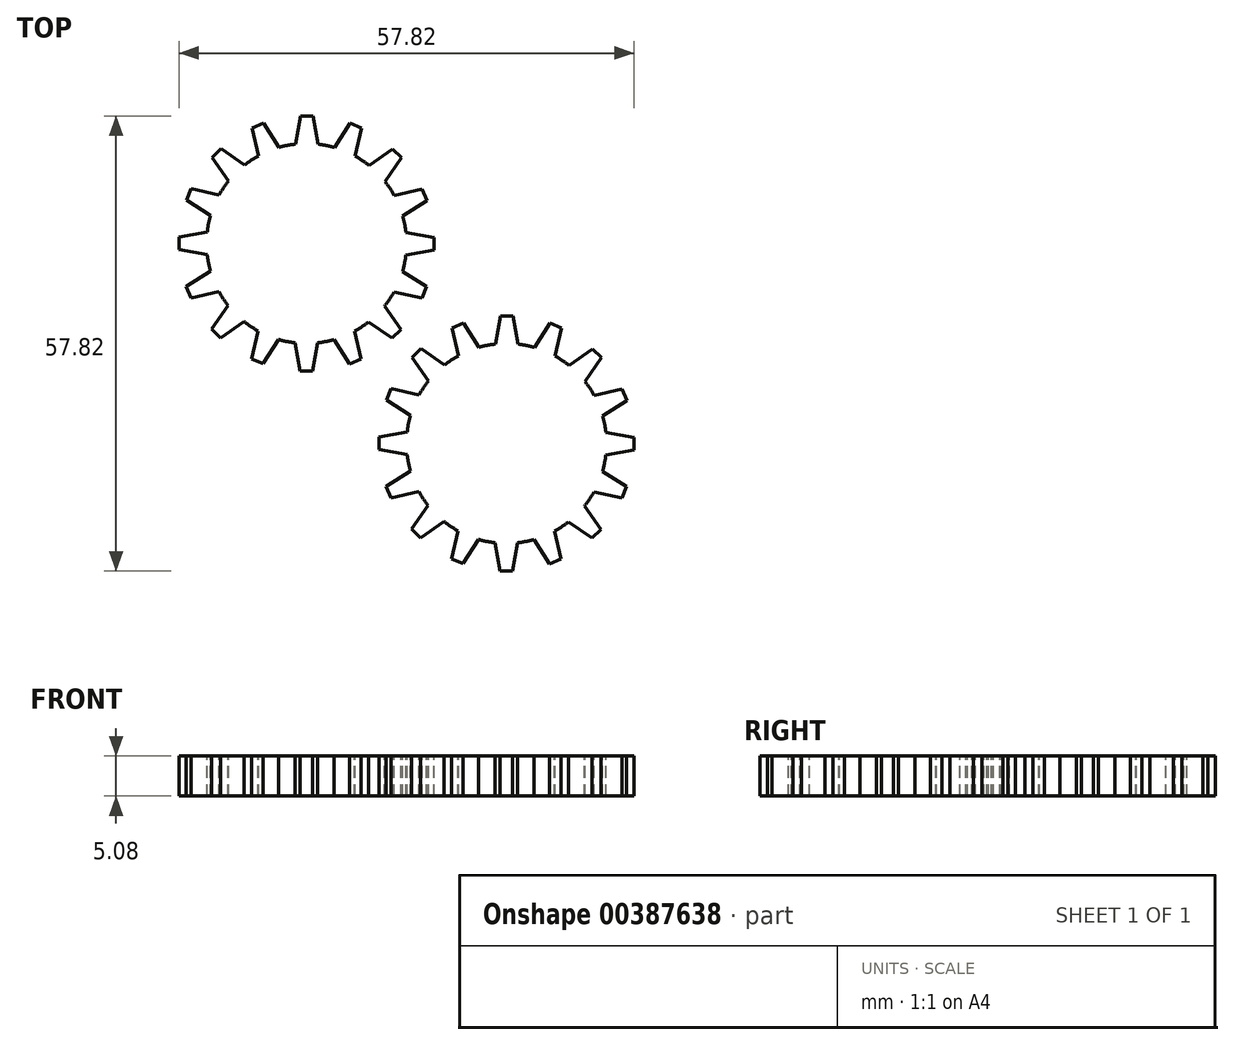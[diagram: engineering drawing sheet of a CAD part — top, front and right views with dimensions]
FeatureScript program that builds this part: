
annotation { "Feature Type Name" : "Feature", "Feature Type Description" : "" }
export const myFeature = defineFeature(function(context is Context, id is Id, definition is map)
    precondition{}
    {
        {
            var Q0;
            Q0=qCreatedBy(makeId("Top.planeOp"),FACE);
            var sketch = newSketch(context, id + "F0", { "sketchPlane" : qUnion([Q0])});
            skArc(sketch, "E0", {"start": v(-6.12, 11.13) * mm, "mid": v(-7.03, 10.58) * mm, "end": v(-7.9, 9.95) * mm});
            skLineSegment(sketch, "E1", {"start": v(-1.4, 12.62) * mm, "end": v(-0.76, 16.2) * mm});
            skLineSegment(sketch, "E2", {"start": v(-0.76, 16.2) * mm, "end": v(0.82, 16.2) * mm});
            skLineSegment(sketch, "E3", {"start": v(0.82, 16.2) * mm, "end": v(1.45, 12.62) * mm});
            skLineSegment(sketch, "E4.1.0", {"start": v(-6.12, 11.13) * mm, "end": v(-6.9, 14.68) * mm});
            skLineSegment(sketch, "E4.1.1", {"start": v(-6.9, 14.68) * mm, "end": v(-5.45, 15.29) * mm});
            skLineSegment(sketch, "E4.1.2", {"start": v(-5.45, 15.29) * mm, "end": v(-3.49, 12.21) * mm});
            skLineSegment(sketch, "E4.2.0", {"start": v(-9.91, 7.94) * mm, "end": v(-12, 10.92) * mm});
            skLineSegment(sketch, "E4.2.1", {"start": v(-12, 10.92) * mm, "end": v(-10.88, 12.04) * mm});
            skLineSegment(sketch, "E4.2.2", {"start": v(-10.88, 12.04) * mm, "end": v(-7.9, 9.95) * mm});
            skLineSegment(sketch, "E5.1.3.0", {"start": v(-12.2, 3.54) * mm, "end": v(-15.27, 5.5) * mm});
            skLineSegment(sketch, "E5.3.3.0", {"start": v(-15.27, 5.5) * mm, "end": v(-14.66, 6.96) * mm});
            skLineSegment(sketch, "E5.6.3.0", {"start": v(-14.66, 6.96) * mm, "end": v(-11.1, 6.17) * mm});
            skLineSegment(sketch, "E5.1.4.0", {"start": v(-12.62, -1.4) * mm, "end": v(-16.2, -0.76) * mm});
            skLineSegment(sketch, "E5.3.4.0", {"start": v(-16.2, -0.76) * mm, "end": v(-16.2, 0.82) * mm});
            skLineSegment(sketch, "E5.6.4.0", {"start": v(-16.2, 0.82) * mm, "end": v(-12.62, 1.45) * mm});
            skLineSegment(sketch, "E5.1.5.0", {"start": v(-11.13, -6.12) * mm, "end": v(-14.68, -6.9) * mm});
            skLineSegment(sketch, "E5.3.5.0", {"start": v(-14.68, -6.9) * mm, "end": v(-15.29, -5.45) * mm});
            skLineSegment(sketch, "E5.6.5.0", {"start": v(-15.29, -5.45) * mm, "end": v(-12.21, -3.49) * mm});
            skLineSegment(sketch, "E6.1.6.0", {"start": v(-7.94, -9.91) * mm, "end": v(-10.92, -12) * mm});
            skLineSegment(sketch, "E6.3.6.0", {"start": v(-10.92, -12) * mm, "end": v(-12.04, -10.88) * mm});
            skLineSegment(sketch, "E6.6.6.0", {"start": v(-12.04, -10.88) * mm, "end": v(-9.95, -7.9) * mm});
            skLineSegment(sketch, "E6.1.7.0", {"start": v(-3.54, -12.2) * mm, "end": v(-5.5, -15.27) * mm});
            skLineSegment(sketch, "E6.3.7.0", {"start": v(-5.5, -15.27) * mm, "end": v(-6.96, -14.66) * mm});
            skLineSegment(sketch, "E6.6.7.0", {"start": v(-6.96, -14.66) * mm, "end": v(-6.17, -11.1) * mm});
            skLineSegment(sketch, "E6.1.8.0", {"start": v(1.4, -12.62) * mm, "end": v(0.76, -16.2) * mm});
            skLineSegment(sketch, "E6.3.8.0", {"start": v(0.76, -16.2) * mm, "end": v(-0.82, -16.2) * mm});
            skLineSegment(sketch, "E6.6.8.0", {"start": v(-0.82, -16.2) * mm, "end": v(-1.45, -12.62) * mm});
            skLineSegment(sketch, "E6.1.9.0", {"start": v(6.12, -11.13) * mm, "end": v(6.9, -14.68) * mm});
            skLineSegment(sketch, "E6.3.9.0", {"start": v(6.9, -14.68) * mm, "end": v(5.45, -15.29) * mm});
            skLineSegment(sketch, "E6.6.9.0", {"start": v(5.45, -15.29) * mm, "end": v(3.49, -12.21) * mm});
            skLineSegment(sketch, "E6.1.10.0", {"start": v(9.91, -7.94) * mm, "end": v(12, -10.92) * mm});
            skLineSegment(sketch, "E6.3.10.0", {"start": v(12, -10.92) * mm, "end": v(10.88, -12.04) * mm});
            skLineSegment(sketch, "E6.6.10.0", {"start": v(10.88, -12.04) * mm, "end": v(7.9, -9.95) * mm});
            skLineSegment(sketch, "E6.1.11.0", {"start": v(12.2, -3.54) * mm, "end": v(15.27, -5.5) * mm});
            skLineSegment(sketch, "E6.3.11.0", {"start": v(15.27, -5.5) * mm, "end": v(14.66, -6.96) * mm});
            skLineSegment(sketch, "E6.6.11.0", {"start": v(14.66, -6.96) * mm, "end": v(11.1, -6.17) * mm});
            skLineSegment(sketch, "E6.1.12.0", {"start": v(12.62, 1.4) * mm, "end": v(16.2, 0.76) * mm});
            skLineSegment(sketch, "E6.3.12.0", {"start": v(16.2, 0.76) * mm, "end": v(16.2, -0.82) * mm});
            skLineSegment(sketch, "E6.6.12.0", {"start": v(16.2, -0.82) * mm, "end": v(12.62, -1.45) * mm});
            skLineSegment(sketch, "E6.1.13.0", {"start": v(11.13, 6.12) * mm, "end": v(14.68, 6.9) * mm});
            skLineSegment(sketch, "E6.3.13.0", {"start": v(14.68, 6.9) * mm, "end": v(15.29, 5.45) * mm});
            skLineSegment(sketch, "E6.6.13.0", {"start": v(15.29, 5.45) * mm, "end": v(12.21, 3.49) * mm});
            skLineSegment(sketch, "E6.1.14.0", {"start": v(7.94, 9.91) * mm, "end": v(10.92, 12) * mm});
            skLineSegment(sketch, "E6.3.14.0", {"start": v(10.92, 12) * mm, "end": v(12.04, 10.88) * mm});
            skLineSegment(sketch, "E6.6.14.0", {"start": v(12.04, 10.88) * mm, "end": v(9.95, 7.9) * mm});
            skLineSegment(sketch, "E6.1.15.0", {"start": v(3.54, 12.2) * mm, "end": v(5.5, 15.27) * mm});
            skLineSegment(sketch, "E6.3.15.0", {"start": v(5.5, 15.27) * mm, "end": v(6.96, 14.66) * mm});
            skLineSegment(sketch, "E6.6.15.0", {"start": v(6.96, 14.66) * mm, "end": v(6.17, 11.1) * mm});
            skArc(sketch, "E7.trimOffspring", {"start": v(-9.91, 7.94) * mm, "mid": v(-10.54, 7.08) * mm, "end": v(-11.1, 6.17) * mm});
            skArc(sketch, "E8.trimOffspring", {"start": v(-12.2, 3.54) * mm, "mid": v(-12.45, 2.5) * mm, "end": v(-12.62, 1.45) * mm});
            skArc(sketch, "E9.trimOffspring", {"start": v(-12.62, -1.4) * mm, "mid": v(-12.46, -2.45) * mm, "end": v(-12.21, -3.49) * mm});
            skArc(sketch, "E10.trimOffspring", {"start": v(-11.13, -6.12) * mm, "mid": v(-10.58, -7.03) * mm, "end": v(-9.95, -7.9) * mm});
            skArc(sketch, "E11.trimOffspring", {"start": v(-7.94, -9.91) * mm, "mid": v(-7.08, -10.54) * mm, "end": v(-6.17, -11.1) * mm});
            skArc(sketch, "E12.trimOffspring", {"start": v(-3.54, -12.2) * mm, "mid": v(-2.5, -12.45) * mm, "end": v(-1.45, -12.62) * mm});
            skArc(sketch, "E13.trimOffspring", {"start": v(1.4, -12.62) * mm, "mid": v(2.45, -12.46) * mm, "end": v(3.49, -12.21) * mm});
            skArc(sketch, "E14.trimOffspring", {"start": v(6.12, -11.13) * mm, "mid": v(7.03, -10.58) * mm, "end": v(7.9, -9.95) * mm});
            skArc(sketch, "E15.trimOffspring", {"start": v(9.91, -7.94) * mm, "mid": v(10.54, -7.08) * mm, "end": v(11.1, -6.17) * mm});
            skArc(sketch, "E16.trimOffspring", {"start": v(12.2, -3.54) * mm, "mid": v(12.45, -2.5) * mm, "end": v(12.62, -1.45) * mm});
            skArc(sketch, "E17.trimOffspring", {"start": v(12.62, 1.4) * mm, "mid": v(12.46, 2.45) * mm, "end": v(12.21, 3.49) * mm});
            skArc(sketch, "E18.trimOffspring", {"start": v(11.13, 6.12) * mm, "mid": v(10.58, 7.03) * mm, "end": v(9.95, 7.9) * mm});
            skArc(sketch, "E19.trimOffspring", {"start": v(7.94, 9.91) * mm, "mid": v(7.08, 10.54) * mm, "end": v(6.17, 11.1) * mm});
            skArc(sketch, "E20.trimOffspring", {"start": v(3.54, 12.2) * mm, "mid": v(2.5, 12.45) * mm, "end": v(1.45, 12.62) * mm});
            skArc(sketch, "E21.trimOffspring", {"start": v(-1.4, 12.62) * mm, "mid": v(-2.45, 12.46) * mm, "end": v(-3.49, 12.21) * mm});
            skSolve(sketch);
        }
        {
            var Q0;
            Q0 = qSketchRegion(id + "F0", true);
            var Q1;
            Q1=sQuery(id+"F0.wireOp",EDGE,"E4.2.2");
            var Q2;
            Q2=sQuery(id+"F0.wireOp",EDGE,"E4.2.1");
            var Q3;
            Q3=sQuery(id+"F0.wireOp",EDGE,"E4.2.0");
            var Q4;
            Q4=sQuery(id+"F0.wireOp",EDGE,"E7.trimOffspring");
            var Q5;
            Q5=sQuery(id+"F0.wireOp",EDGE,"E5.6.3.0");
            var Q6;
            Q6=sQuery(id+"F0.wireOp",EDGE,"E5.3.3.0");
            var Q7;
            Q7=sQuery(id+"F0.wireOp",EDGE,"E5.1.3.0");
            var Q8;
            Q8=sQuery(id+"F0.wireOp",EDGE,"E8.trimOffspring");
            var Q9;
            Q9=sQuery(id+"F0.wireOp",EDGE,"E5.6.4.0");
            var Q10;
            Q10=sQuery(id+"F0.wireOp",EDGE,"E5.3.4.0");
            var Q11;
            Q11=sQuery(id+"F0.wireOp",EDGE,"E5.1.4.0");
            var Q12;
            Q12=sQuery(id+"F0.wireOp",EDGE,"E9.trimOffspring");
            var Q13;
            Q13=sQuery(id+"F0.wireOp",EDGE,"E5.6.5.0");
            var Q14;
            Q14=sQuery(id+"F0.wireOp",EDGE,"E5.3.5.0");
            var Q15;
            Q15=sQuery(id+"F0.wireOp",EDGE,"E5.1.5.0");
            var Q16;
            Q16=sQuery(id+"F0.wireOp",EDGE,"E10.trimOffspring");
            var Q17;
            Q17=sQuery(id+"F0.wireOp",EDGE,"E6.6.6.0");
            var Q18;
            Q18=sQuery(id+"F0.wireOp",EDGE,"E6.3.6.0");
            var Q19;
            Q19=sQuery(id+"F0.wireOp",EDGE,"E6.1.6.0");
            var Q20;
            Q20=sQuery(id+"F0.wireOp",EDGE,"E11.trimOffspring");
            var Q21;
            Q21=sQuery(id+"F0.wireOp",EDGE,"E6.6.7.0");
            var Q22;
            Q22=sQuery(id+"F0.wireOp",EDGE,"E6.3.7.0");
            var Q23;
            Q23=sQuery(id+"F0.wireOp",EDGE,"E6.1.7.0");
            var Q24;
            Q24=sQuery(id+"F0.wireOp",EDGE,"E12.trimOffspring");
            var Q25;
            Q25=sQuery(id+"F0.wireOp",EDGE,"E6.6.8.0");
            var Q26;
            Q26=sQuery(id+"F0.wireOp",EDGE,"E6.3.8.0");
            var Q27;
            Q27=sQuery(id+"F0.wireOp",EDGE,"E6.1.8.0");
            var Q28;
            Q28=sQuery(id+"F0.wireOp",EDGE,"E13.trimOffspring");
            var Q29;
            Q29=sQuery(id+"F0.wireOp",EDGE,"E6.6.9.0");
            var Q30;
            Q30=sQuery(id+"F0.wireOp",EDGE,"E6.3.9.0");
            var Q31;
            Q31=sQuery(id+"F0.wireOp",EDGE,"E14.trimOffspring");
            var Q32;
            Q32=sQuery(id+"F0.wireOp",EDGE,"E6.3.10.0");
            var Q33;
            Q33=sQuery(id+"F0.wireOp",EDGE,"E6.6.10.0");
            var Q34;
            Q34=sQuery(id+"F0.wireOp",EDGE,"E6.1.10.0");
            var Q35;
            Q35=sQuery(id+"F0.wireOp",EDGE,"E15.trimOffspring");
            var Q36;
            Q36=sQuery(id+"F0.wireOp",EDGE,"E6.6.11.0");
            var Q37;
            Q37=sQuery(id+"F0.wireOp",EDGE,"E6.3.11.0");
            var Q38;
            Q38=sQuery(id+"F0.wireOp",EDGE,"E6.1.11.0");
            var Q39;
            Q39=sQuery(id+"F0.wireOp",EDGE,"E16.trimOffspring");
            var Q40;
            Q40=sQuery(id+"F0.wireOp",EDGE,"E6.6.12.0");
            var Q41;
            Q41=sQuery(id+"F0.wireOp",EDGE,"E6.3.12.0");
            var Q42;
            Q42=sQuery(id+"F0.wireOp",EDGE,"E6.1.12.0");
            var Q43;
            Q43=sQuery(id+"F0.wireOp",EDGE,"E17.trimOffspring");
            var Q44;
            Q44=sQuery(id+"F0.wireOp",EDGE,"E6.6.13.0");
            var Q45;
            Q45=sQuery(id+"F0.wireOp",EDGE,"E6.3.13.0");
            var Q46;
            Q46=sQuery(id+"F0.wireOp",EDGE,"E6.1.13.0");
            var Q47;
            Q47=sQuery(id+"F0.wireOp",EDGE,"E18.trimOffspring");
            var Q48;
            Q48=sQuery(id+"F0.wireOp",EDGE,"E6.6.14.0");
            var Q49;
            Q49=sQuery(id+"F0.wireOp",EDGE,"E6.3.14.0");
            var Q50;
            Q50=sQuery(id+"F0.wireOp",EDGE,"E19.trimOffspring");
            var Q51;
            Q51=sQuery(id+"F0.wireOp",EDGE,"E6.6.15.0");
            var Q52;
            Q52=sQuery(id+"F0.wireOp",EDGE,"E6.1.14.0");
            var Q53;
            Q53=sQuery(id+"F0.wireOp",EDGE,"E6.3.15.0");
            var Q54;
            Q54=sQuery(id+"F0.wireOp",EDGE,"E6.1.15.0");
            var Q55;
            Q55=sQuery(id+"F0.wireOp",EDGE,"E20.trimOffspring");
            var Q56;
            Q56=sQuery(id+"F0.wireOp",EDGE,"E3");
            var Q57;
            Q57=sQuery(id+"F0.wireOp",EDGE,"E2");
            var Q58;
            Q58=sQuery(id+"F0.wireOp",EDGE,"E1");
            var Q59;
            Q59=sQuery(id+"F0.wireOp",EDGE,"E21.trimOffspring");
            var Q60;
            Q60=sQuery(id+"F0.wireOp",EDGE,"E4.1.2");
            var Q61;
            Q61=sQuery(id+"F0.wireOp",EDGE,"E4.1.1");
            var Q62;
            Q62=sQuery(id+"F0.wireOp",EDGE,"E4.1.0");
            var Q63;
            Q63=sQuery(id+"F0.wireOp",EDGE,"E0");
            var Q64;
            Q64=sQuery(id+"F0.wireOp",EDGE,"E6.1.9.0");
            extrude(context, id + "F1", {"entities" : qUnion([Q0]), "bodyType" : ToolBodyType.SURFACE, "surfaceEntities" : qUnion([Q1, Q2, Q3, Q4, Q5, Q6, Q7, Q8, Q9, Q10, Q11, Q12, Q13, Q14, Q15, Q16, Q17, Q18, Q19, Q20, Q21, Q22, Q23, Q24, Q25, Q26, Q27, Q28, Q29, Q30, Q31, Q32, Q33, Q34, Q35, Q36, Q37, Q38, Q39, Q40, Q41, Q42, Q43, Q44, Q45, Q46, Q47, Q48, Q49, Q50, Q51, Q52, Q53, Q54, Q55, Q56, Q57, Q58, Q59, Q60, Q61, Q62, Q63, Q64]), "depth" : 5.08 * mm, "offsetDistance" : 25.4 * mm});
        }
        {
            var Q0;
            Q0=qCreatedBy(makeId("Top.planeOp"),FACE);
            var sketch = newSketch(context, id + "F2", { "sketchPlane" : qUnion([Q0])});
            skArc(sketch, "E22", {"start": v(-31.52, 36.53) * mm, "mid": v(-32.43, 35.98) * mm, "end": v(-33.3, 35.35) * mm});
            skLineSegment(sketch, "E23", {"start": v(-26.8, 38.02) * mm, "end": v(-26.16, 41.6) * mm});
            skLineSegment(sketch, "E24", {"start": v(-26.16, 41.6) * mm, "end": v(-24.58, 41.6) * mm});
            skLineSegment(sketch, "E25", {"start": v(-24.58, 41.6) * mm, "end": v(-23.95, 38.02) * mm});
            skLineSegment(sketch, "E26.1.0", {"start": v(-31.52, 36.53) * mm, "end": v(-32.3, 40.08) * mm});
            skLineSegment(sketch, "E26.1.1", {"start": v(-32.3, 40.08) * mm, "end": v(-30.85, 40.69) * mm});
            skLineSegment(sketch, "E26.1.2", {"start": v(-30.85, 40.69) * mm, "end": v(-28.89, 37.61) * mm});
            skLineSegment(sketch, "E26.2.0", {"start": v(-35.31, 33.34) * mm, "end": v(-37.4, 36.32) * mm});
            skLineSegment(sketch, "E26.2.1", {"start": v(-37.4, 36.32) * mm, "end": v(-36.28, 37.44) * mm});
            skLineSegment(sketch, "E26.2.2", {"start": v(-36.28, 37.44) * mm, "end": v(-33.3, 35.35) * mm});
            skLineSegment(sketch, "E27.1.3.0", {"start": v(-37.6, 28.94) * mm, "end": v(-40.67, 30.9) * mm});
            skLineSegment(sketch, "E27.3.3.0", {"start": v(-40.67, 30.9) * mm, "end": v(-40.06, 32.36) * mm});
            skLineSegment(sketch, "E27.6.3.0", {"start": v(-40.06, 32.36) * mm, "end": v(-36.5, 31.57) * mm});
            skLineSegment(sketch, "E27.1.4.0", {"start": v(-38.02, 24) * mm, "end": v(-41.6, 24.64) * mm});
            skLineSegment(sketch, "E27.3.4.0", {"start": v(-41.6, 24.64) * mm, "end": v(-41.6, 26.22) * mm});
            skLineSegment(sketch, "E27.6.4.0", {"start": v(-41.6, 26.22) * mm, "end": v(-38.02, 26.85) * mm});
            skLineSegment(sketch, "E27.1.5.0", {"start": v(-36.53, 19.28) * mm, "end": v(-40.08, 18.5) * mm});
            skLineSegment(sketch, "E27.3.5.0", {"start": v(-40.08, 18.5) * mm, "end": v(-40.69, 19.95) * mm});
            skLineSegment(sketch, "E27.6.5.0", {"start": v(-40.69, 19.95) * mm, "end": v(-37.61, 21.91) * mm});
            skLineSegment(sketch, "E28.1.6.0", {"start": v(-33.34, 15.49) * mm, "end": v(-36.32, 13.4) * mm});
            skLineSegment(sketch, "E28.3.6.0", {"start": v(-36.32, 13.4) * mm, "end": v(-37.44, 14.52) * mm});
            skLineSegment(sketch, "E28.6.6.0", {"start": v(-37.44, 14.52) * mm, "end": v(-35.35, 17.5) * mm});
            skLineSegment(sketch, "E28.1.7.0", {"start": v(-28.94, 13.2) * mm, "end": v(-30.9, 10.13) * mm});
            skLineSegment(sketch, "E28.3.7.0", {"start": v(-30.9, 10.13) * mm, "end": v(-32.36, 10.74) * mm});
            skLineSegment(sketch, "E28.6.7.0", {"start": v(-32.36, 10.74) * mm, "end": v(-31.57, 14.3) * mm});
            skLineSegment(sketch, "E28.1.8.0", {"start": v(-24, 12.78) * mm, "end": v(-24.64, 9.2) * mm});
            skLineSegment(sketch, "E28.3.8.0", {"start": v(-24.64, 9.2) * mm, "end": v(-26.22, 9.2) * mm});
            skLineSegment(sketch, "E28.6.8.0", {"start": v(-26.22, 9.2) * mm, "end": v(-26.85, 12.78) * mm});
            skLineSegment(sketch, "E28.1.9.0", {"start": v(-19.28, 14.27) * mm, "end": v(-18.5, 10.72) * mm});
            skLineSegment(sketch, "E28.3.9.0", {"start": v(-18.5, 10.72) * mm, "end": v(-19.95, 10.11) * mm});
            skLineSegment(sketch, "E28.6.9.0", {"start": v(-19.95, 10.11) * mm, "end": v(-21.91, 13.19) * mm});
            skLineSegment(sketch, "E28.1.10.0", {"start": v(-15.49, 17.46) * mm, "end": v(-13.4, 14.48) * mm});
            skLineSegment(sketch, "E28.3.10.0", {"start": v(-13.4, 14.48) * mm, "end": v(-14.52, 13.36) * mm});
            skLineSegment(sketch, "E28.6.10.0", {"start": v(-14.52, 13.36) * mm, "end": v(-17.5, 15.45) * mm});
            skLineSegment(sketch, "E28.1.11.0", {"start": v(-13.2, 21.86) * mm, "end": v(-10.13, 19.9) * mm});
            skLineSegment(sketch, "E28.3.11.0", {"start": v(-10.13, 19.9) * mm, "end": v(-10.74, 18.44) * mm});
            skLineSegment(sketch, "E28.6.11.0", {"start": v(-10.74, 18.44) * mm, "end": v(-14.3, 19.23) * mm});
            skLineSegment(sketch, "E28.1.12.0", {"start": v(-12.78, 26.8) * mm, "end": v(-9.2, 26.16) * mm});
            skLineSegment(sketch, "E28.3.12.0", {"start": v(-9.2, 26.16) * mm, "end": v(-9.2, 24.58) * mm});
            skLineSegment(sketch, "E28.6.12.0", {"start": v(-9.2, 24.58) * mm, "end": v(-12.78, 23.95) * mm});
            skLineSegment(sketch, "E28.1.13.0", {"start": v(-14.27, 31.52) * mm, "end": v(-10.72, 32.3) * mm});
            skLineSegment(sketch, "E28.3.13.0", {"start": v(-10.72, 32.3) * mm, "end": v(-10.11, 30.85) * mm});
            skLineSegment(sketch, "E28.6.13.0", {"start": v(-10.11, 30.85) * mm, "end": v(-13.19, 28.89) * mm});
            skLineSegment(sketch, "E28.1.14.0", {"start": v(-17.46, 35.31) * mm, "end": v(-14.48, 37.4) * mm});
            skLineSegment(sketch, "E28.3.14.0", {"start": v(-14.48, 37.4) * mm, "end": v(-13.36, 36.28) * mm});
            skLineSegment(sketch, "E28.6.14.0", {"start": v(-13.36, 36.28) * mm, "end": v(-15.45, 33.3) * mm});
            skLineSegment(sketch, "E28.1.15.0", {"start": v(-21.86, 37.6) * mm, "end": v(-19.9, 40.67) * mm});
            skLineSegment(sketch, "E28.3.15.0", {"start": v(-19.9, 40.67) * mm, "end": v(-18.44, 40.06) * mm});
            skLineSegment(sketch, "E28.6.15.0", {"start": v(-18.44, 40.06) * mm, "end": v(-19.23, 36.5) * mm});
            skArc(sketch, "E29.trimOffspring", {"start": v(-35.31, 33.34) * mm, "mid": v(-35.94, 32.48) * mm, "end": v(-36.5, 31.57) * mm});
            skArc(sketch, "E30.trimOffspring", {"start": v(-37.6, 28.94) * mm, "mid": v(-37.85, 27.9) * mm, "end": v(-38.02, 26.85) * mm});
            skArc(sketch, "E31.trimOffspring", {"start": v(-38.02, 24) * mm, "mid": v(-37.86, 22.95) * mm, "end": v(-37.61, 21.91) * mm});
            skArc(sketch, "E32.trimOffspring", {"start": v(-36.53, 19.28) * mm, "mid": v(-35.98, 18.37) * mm, "end": v(-35.35, 17.5) * mm});
            skArc(sketch, "E33.trimOffspring", {"start": v(-33.34, 15.49) * mm, "mid": v(-32.48, 14.86) * mm, "end": v(-31.57, 14.3) * mm});
            skArc(sketch, "E34.trimOffspring", {"start": v(-28.94, 13.2) * mm, "mid": v(-27.9, 12.95) * mm, "end": v(-26.85, 12.78) * mm});
            skArc(sketch, "E35.trimOffspring", {"start": v(-24, 12.78) * mm, "mid": v(-22.95, 12.94) * mm, "end": v(-21.91, 13.19) * mm});
            skArc(sketch, "E36.trimOffspring", {"start": v(-19.28, 14.27) * mm, "mid": v(-18.37, 14.82) * mm, "end": v(-17.5, 15.45) * mm});
            skArc(sketch, "E37.trimOffspring", {"start": v(-15.49, 17.46) * mm, "mid": v(-14.86, 18.32) * mm, "end": v(-14.3, 19.23) * mm});
            skArc(sketch, "E38.trimOffspring", {"start": v(-13.2, 21.86) * mm, "mid": v(-12.95, 22.9) * mm, "end": v(-12.78, 23.95) * mm});
            skArc(sketch, "E39.trimOffspring", {"start": v(-12.78, 26.8) * mm, "mid": v(-12.94, 27.85) * mm, "end": v(-13.19, 28.89) * mm});
            skArc(sketch, "E40.trimOffspring", {"start": v(-14.27, 31.52) * mm, "mid": v(-14.82, 32.43) * mm, "end": v(-15.45, 33.3) * mm});
            skArc(sketch, "E41.trimOffspring", {"start": v(-17.46, 35.31) * mm, "mid": v(-18.32, 35.94) * mm, "end": v(-19.23, 36.5) * mm});
            skArc(sketch, "E42.trimOffspring", {"start": v(-21.86, 37.6) * mm, "mid": v(-22.9, 37.85) * mm, "end": v(-23.95, 38.02) * mm});
            skArc(sketch, "E43.trimOffspring", {"start": v(-26.8, 38.02) * mm, "mid": v(-27.85, 37.86) * mm, "end": v(-28.89, 37.61) * mm});
            skSolve(sketch);
        }
        {
            var Q0;
            Q0 = qSketchRegion(id + "F2", true);
            var Q1;
            Q1=sQuery(id+"F2.wireOp",EDGE,"E28.1.6.0");
            var Q2;
            Q2=sQuery(id+"F2.wireOp",EDGE,"E28.6.10.0");
            var Q3;
            Q3=sQuery(id+"F2.wireOp",EDGE,"E28.1.14.0");
            var Q4;
            Q4=sQuery(id+"F2.wireOp",EDGE,"E26.2.0");
            var Q5;
            Q5=sQuery(id+"F2.wireOp",EDGE,"E23");
            var Q6;
            Q6=sQuery(id+"F2.wireOp",EDGE,"E28.6.15.0");
            var Q7;
            Q7=sQuery(id+"F2.wireOp",EDGE,"E26.1.0");
            var Q8;
            Q8=sQuery(id+"F2.wireOp",EDGE,"E27.6.3.0");
            var Q9;
            Q9=sQuery(id+"F2.wireOp",EDGE,"E28.1.8.0");
            var Q10;
            Q10=sQuery(id+"F2.wireOp",EDGE,"E37.trimOffspring");
            var Q11;
            Q11=sQuery(id+"F2.wireOp",EDGE,"E27.1.5.0");
            var Q12;
            Q12=sQuery(id+"F2.wireOp",EDGE,"E26.2.2");
            var Q13;
            Q13=sQuery(id+"F2.wireOp",EDGE,"E28.1.9.0");
            var Q14;
            Q14=sQuery(id+"F2.wireOp",EDGE,"E25");
            var Q15;
            Q15=sQuery(id+"F2.wireOp",EDGE,"E28.6.6.0");
            var Q16;
            Q16=sQuery(id+"F2.wireOp",EDGE,"E27.6.4.0");
            var Q17;
            Q17=sQuery(id+"F2.wireOp",EDGE,"E28.6.8.0");
            var Q18;
            Q18=sQuery(id+"F2.wireOp",EDGE,"E28.1.15.0");
            var Q19;
            Q19=sQuery(id+"F2.wireOp",EDGE,"E28.6.7.0");
            var Q20;
            Q20=sQuery(id+"F2.wireOp",EDGE,"E40.trimOffspring");
            var Q21;
            Q21=sQuery(id+"F2.wireOp",EDGE,"E26.1.2");
            var Q22;
            Q22=sQuery(id+"F2.wireOp",EDGE,"E27.1.4.0");
            var Q23;
            Q23=sQuery(id+"F2.wireOp",EDGE,"E41.trimOffspring");
            var Q24;
            Q24=sQuery(id+"F2.wireOp",EDGE,"E30.trimOffspring");
            var Q25;
            Q25=sQuery(id+"F2.wireOp",EDGE,"E28.3.8.0");
            var Q26;
            Q26=sQuery(id+"F2.wireOp",EDGE,"E27.1.3.0");
            var Q27;
            Q27=sQuery(id+"F2.wireOp",EDGE,"E26.2.1");
            var Q28;
            Q28=sQuery(id+"F2.wireOp",EDGE,"E27.6.5.0");
            var Q29;
            Q29=sQuery(id+"F2.wireOp",EDGE,"E34.trimOffspring");
            var Q30;
            Q30=sQuery(id+"F2.wireOp",EDGE,"E32.trimOffspring");
            var Q31;
            Q31=sQuery(id+"F2.wireOp",EDGE,"E27.3.5.0");
            var Q32;
            Q32=sQuery(id+"F2.wireOp",EDGE,"E36.trimOffspring");
            var Q33;
            Q33=sQuery(id+"F2.wireOp",EDGE,"E31.trimOffspring");
            var Q34;
            Q34=sQuery(id+"F2.wireOp",EDGE,"E33.trimOffspring");
            var Q35;
            Q35=sQuery(id+"F2.wireOp",EDGE,"E28.3.15.0");
            var Q36;
            Q36=sQuery(id+"F2.wireOp",EDGE,"E28.3.6.0");
            var Q37;
            Q37=sQuery(id+"F2.wireOp",EDGE,"E43.trimOffspring");
            var Q38;
            Q38=sQuery(id+"F2.wireOp",EDGE,"E28.1.7.0");
            var Q39;
            Q39=sQuery(id+"F2.wireOp",EDGE,"E28.6.9.0");
            var Q40;
            Q40=sQuery(id+"F2.wireOp",EDGE,"E29.trimOffspring");
            var Q41;
            Q41=sQuery(id+"F2.wireOp",EDGE,"E22");
            var Q42;
            Q42=sQuery(id+"F2.wireOp",EDGE,"E28.3.7.0");
            var Q43;
            Q43=sQuery(id+"F2.wireOp",EDGE,"E35.trimOffspring");
            var Q44;
            Q44=sQuery(id+"F2.wireOp",EDGE,"E26.1.1");
            var Q45;
            Q45=sQuery(id+"F2.wireOp",EDGE,"E27.3.3.0");
            var Q46;
            Q46=sQuery(id+"F2.wireOp",EDGE,"E28.3.9.0");
            var Q47;
            Q47=sQuery(id+"F2.wireOp",EDGE,"E27.3.4.0");
            var Q48;
            Q48=sQuery(id+"F2.wireOp",EDGE,"E42.trimOffspring");
            var Q49;
            Q49=sQuery(id+"F2.wireOp",EDGE,"E24");
            var Q50;
            Q50=sQuery(id+"F2.wireOp",EDGE,"E28.3.14.0");
            var Q51;
            Q51=sQuery(id+"F2.wireOp",EDGE,"E28.1.10.0");
            var Q52;
            Q52=sQuery(id+"F2.wireOp",EDGE,"E28.3.10.0");
            var Q53;
            Q53=sQuery(id+"F2.wireOp",EDGE,"E28.1.13.0");
            var Q54;
            Q54=sQuery(id+"F2.wireOp",EDGE,"E28.6.11.0");
            var Q55;
            Q55=sQuery(id+"F2.wireOp",EDGE,"E28.3.11.0");
            var Q56;
            Q56=sQuery(id+"F2.wireOp",EDGE,"E28.1.11.0");
            var Q57;
            Q57=sQuery(id+"F2.wireOp",EDGE,"E28.6.12.0");
            var Q58;
            Q58=sQuery(id+"F2.wireOp",EDGE,"E28.3.12.0");
            var Q59;
            Q59=sQuery(id+"F2.wireOp",EDGE,"E28.1.12.0");
            var Q60;
            Q60=sQuery(id+"F2.wireOp",EDGE,"E38.trimOffspring");
            var Q61;
            Q61=sQuery(id+"F2.wireOp",EDGE,"E39.trimOffspring");
            var Q62;
            Q62=sQuery(id+"F2.wireOp",EDGE,"E28.6.13.0");
            var Q63;
            Q63=sQuery(id+"F2.wireOp",EDGE,"E28.3.13.0");
            var Q64;
            Q64=sQuery(id+"F2.wireOp",EDGE,"E28.6.14.0");
            extrude(context, id + "F3", {"entities" : qUnion([Q0]), "bodyType" : ToolBodyType.SURFACE, "surfaceEntities" : qUnion([Q1, Q2, Q3, Q4, Q5, Q6, Q7, Q8, Q9, Q10, Q11, Q12, Q13, Q14, Q15, Q16, Q17, Q18, Q19, Q20, Q21, Q22, Q23, Q24, Q25, Q26, Q27, Q28, Q29, Q30, Q31, Q32, Q33, Q34, Q35, Q36, Q37, Q38, Q39, Q40, Q41, Q42, Q43, Q44, Q45, Q46, Q47, Q48, Q49, Q50, Q51, Q52, Q53, Q54, Q55, Q56, Q57, Q58, Q59, Q60, Q61, Q62, Q63, Q64]), "depth" : 5.08 * mm, "offsetDistance" : 25.4 * mm});
        }
    });
